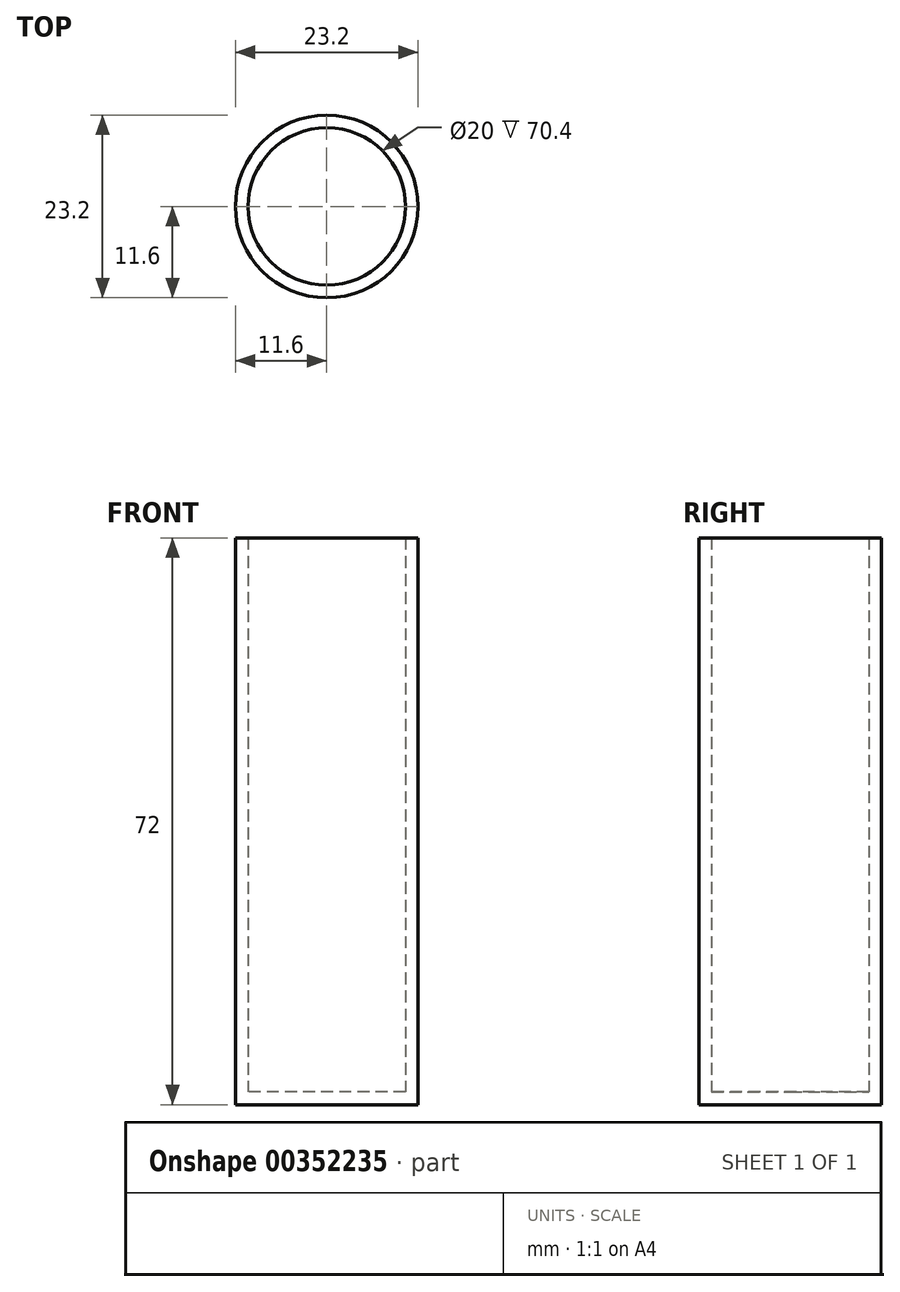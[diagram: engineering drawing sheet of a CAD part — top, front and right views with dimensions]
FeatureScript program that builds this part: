
annotation { "Feature Type Name" : "Feature", "Feature Type Description" : "" }
export const myFeature = defineFeature(function(context is Context, id is Id, definition is map)
    precondition{}
    {
        {
            assignVariable(context, id + "F0", {"name" : "b", "anyValue" : 0.4 * 4});
        }
        {
            var Q0;
            Q0=qCreatedBy(makeId("Top.planeOp"),FACE);
            var sketch = newSketch(context, id + "F1", { "sketchPlane" : qUnion([Q0])});
            skCircle(sketch, "E0", {"center": v(0, 0) * mm, "radius": 11.6 * mm});
            skCircle(sketch, "E1", {"center": v(0, 0) * mm, "radius": 10 * mm});
            skSolve(sketch);
        }
        {
            var Q0;
            Q0=makeQuery(id+"F1.imprint","IMPRINT",FACE,{"disambiguationData":[TD([[makeQuery(id+"F1.imprint","IMPRINT",EDGE,{"derivedFrom":sQuery(id+"F1.wireOp",EDGE,"E1")}),1.0]])]});
            extrude(context, id + "F2", {"entities" : qUnion([Q0]), "depth" : (getVariable(context, 'b')) * mm});
        }
        {
            var Q0;
            Q0=makeQuery(id+"F1.imprint","IMPRINT",FACE,{"disambiguationData":[TD([[makeQuery(id+"F1.imprint","IMPRINT",EDGE,{"derivedFrom":sQuery(id+"F1.wireOp",EDGE,"E0")}),1.0]])]});
            extrude(context, id + "F3", {"entities" : qUnion([Q0]), "operationType" : NewBodyOperationType.ADD, "depth" : 72 * mm});
        }
    });
